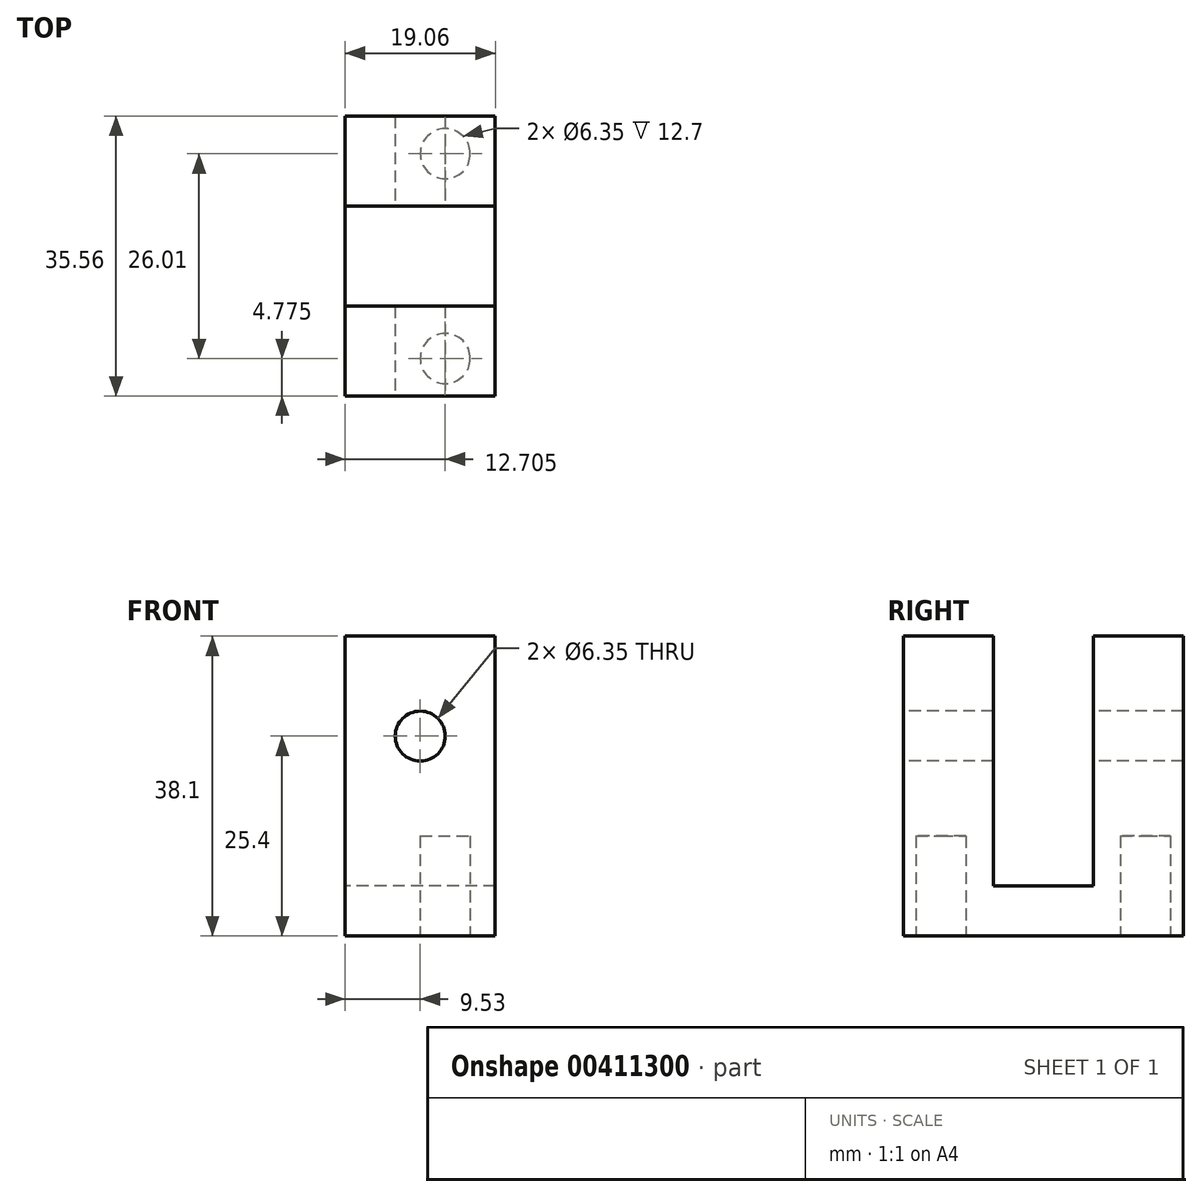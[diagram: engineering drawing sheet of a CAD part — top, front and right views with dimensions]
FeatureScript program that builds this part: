
annotation { "Feature Type Name" : "Feature", "Feature Type Description" : "" }
export const myFeature = defineFeature(function(context is Context, id is Id, definition is map)
    precondition{}
    {
        {
            var Q0;
            Q0=qCreatedBy(makeId("Right.planeOp"),FACE);
            var sketch = newSketch(context, id + "F0", { "sketchPlane" : qUnion([Q0])});
            skLineSegment(sketch, "E0", {"start": v(-17.78, 12.7) * mm, "end": v(-17.78, -25.4) * mm});
            skLineSegment(sketch, "E1", {"start": v(-17.78, -25.4) * mm, "end": v(17.78, -25.4) * mm});
            skLineSegment(sketch, "E2", {"start": v(17.78, -25.4) * mm, "end": v(17.78, 12.7) * mm});
            skLineSegment(sketch, "E3", {"start": v(17.78, 12.7) * mm, "end": v(6.35, 12.7) * mm});
            skLineSegment(sketch, "E4", {"start": v(6.35, 12.7) * mm, "end": v(6.35, -19.05) * mm});
            skLineSegment(sketch, "E5", {"start": v(6.35, -19.05) * mm, "end": v(-6.35, -19.05) * mm});
            skLineSegment(sketch, "E6", {"start": v(-6.35, -19.05) * mm, "end": v(-6.35, 12.7) * mm});
            skLineSegment(sketch, "E7", {"start": v(-6.35, 12.7) * mm, "end": v(-17.78, 12.7) * mm});
            skLineSegment(sketch, "E8", {"start": v(0, 0) * mm, "end": v(0, 7.78) * mm, "construction": true});
            skSolve(sketch);
        }
        {
            var Q0;
            Q0=makeQuery(id+"F0.imprint","IMPRINT",FACE,{"disambiguationData":[TD([[makeQuery(id+"F0.imprint","IMPRINT",EDGE,{"derivedFrom":sQuery(id+"F0.wireOp",EDGE,"E0")}),1.0]])]});
            extrude(context, id + "F1", {"entities" : qUnion([Q0]), "depth" : 19.05 * mm, "symmetric" : true});
        }
        {
            var Q0;
            Q0=qCreatedBy(makeId("Front.planeOp"),FACE);
            var sketch = newSketch(context, id + "F2", { "sketchPlane" : qUnion([Q0])});
            skCircle(sketch, "E9", {"center": v(0, 0) * mm, "radius": 3.18 * mm});
            skSolve(sketch);
        }
        {
            var Q0;
            Q0 = qSketchRegion(id + "F2", true);
            extrude(context, id + "F3", {"entities" : qUnion([Q0]), "operationType" : NewBodyOperationType.REMOVE, "oppositeDirection" : true, "depth" : 35.56 * mm, "symmetric" : true});
        }
        {
            var Q0;
            Q0=makeQuery(id+"F1.opExtrude","SWEPT_FACE",FACE,{"disambiguationData":[OSD([sQuery(id+"F0.wireOp",EDGE,"E1")])]});
            var sketch = newSketch(context, id + "F4", { "sketchPlane" : qUnion([Q0])});
            skCircle(sketch, "E10", {"center": v(3.17, 13) * mm, "radius": 3.18 * mm});
            skCircle(sketch, "E11", {"center": v(3.18, -13) * mm, "radius": 3.17 * mm});
            skSolve(sketch);
        }
        {
            var Q0;
            Q0 = qSketchRegion(id + "F4", true);
            extrude(context, id + "F5", {"entities" : qUnion([Q0]), "operationType" : NewBodyOperationType.REMOVE, "oppositeDirection" : true, "depth" : 12.7 * mm});
        }
    });
